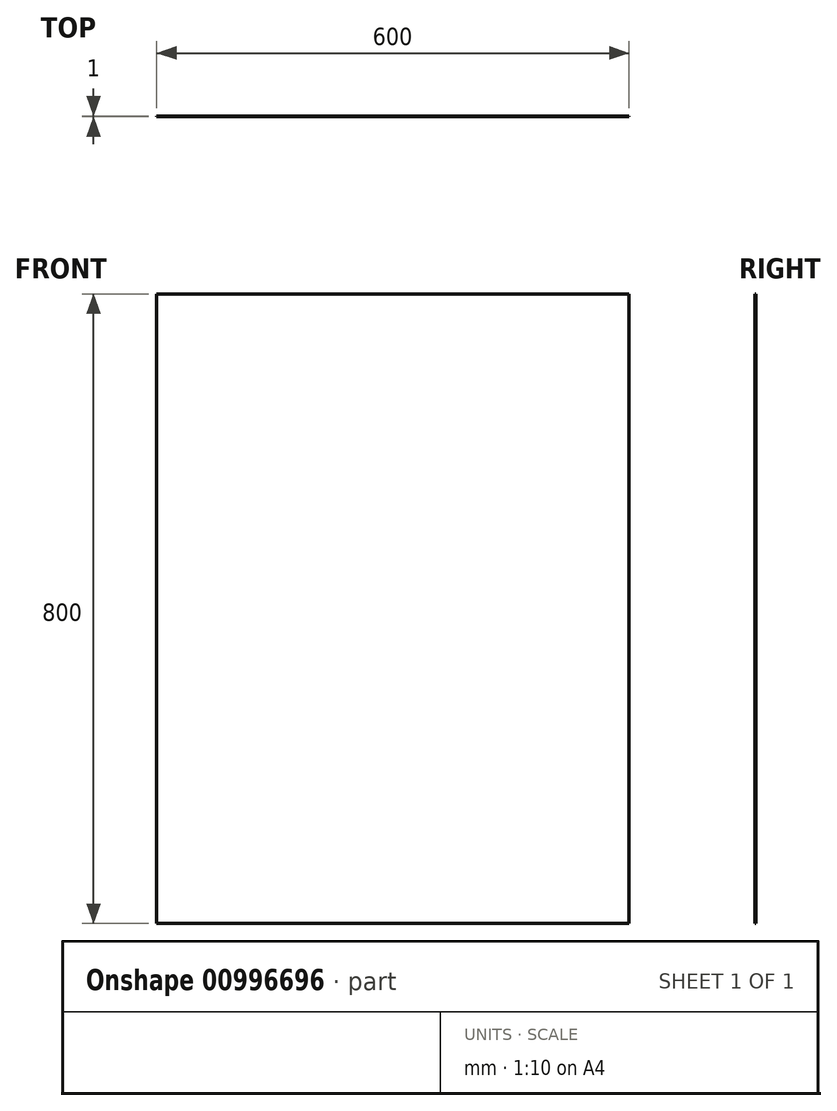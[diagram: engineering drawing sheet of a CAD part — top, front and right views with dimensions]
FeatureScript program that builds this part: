
annotation { "Feature Type Name" : "Feature", "Feature Type Description" : "" }
export const myFeature = defineFeature(function(context is Context, id is Id, definition is map)
    precondition{}
    {
        {
            var Q0;
            Q0=qCreatedBy(makeId("Front.planeOp"),FACE);
            var sketch = newSketch(context, id + "F0", { "sketchPlane" : qUnion([Q0])});
            skLineSegment(sketch, "E0.bottom", {"start": v(300, -400) * mm, "end": v(-300, -400) * mm});
            skLineSegment(sketch, "E0.top", {"start": v(300, 400) * mm, "end": v(-300, 400) * mm});
            skLineSegment(sketch, "E0.left", {"start": v(300, -400) * mm, "end": v(300, 400) * mm});
            skLineSegment(sketch, "E0.right", {"start": v(-300, -400) * mm, "end": v(-300, 400) * mm});
            skPoint(sketch, "E0.middle", {"position": v(0, 0) * mm});
            skSolve(sketch);
        }
        {
            var Q0;
            Q0=makeQuery(id+"F0.imprint","IMPRINT",FACE,{"disambiguationData":[TD([[makeQuery(id+"F0.imprint","IMPRINT",EDGE,{"derivedFrom":sQuery(id+"F0.wireOp",EDGE,"E0.bottom")}),-1.0]])]});
            extrude(context, id + "F1", {"entities" : qUnion([Q0]), "endBound" : BoundingType.SYMMETRIC, "depth" : 1 * mm, "offsetDistance" : 25 * mm});
        }
    });
